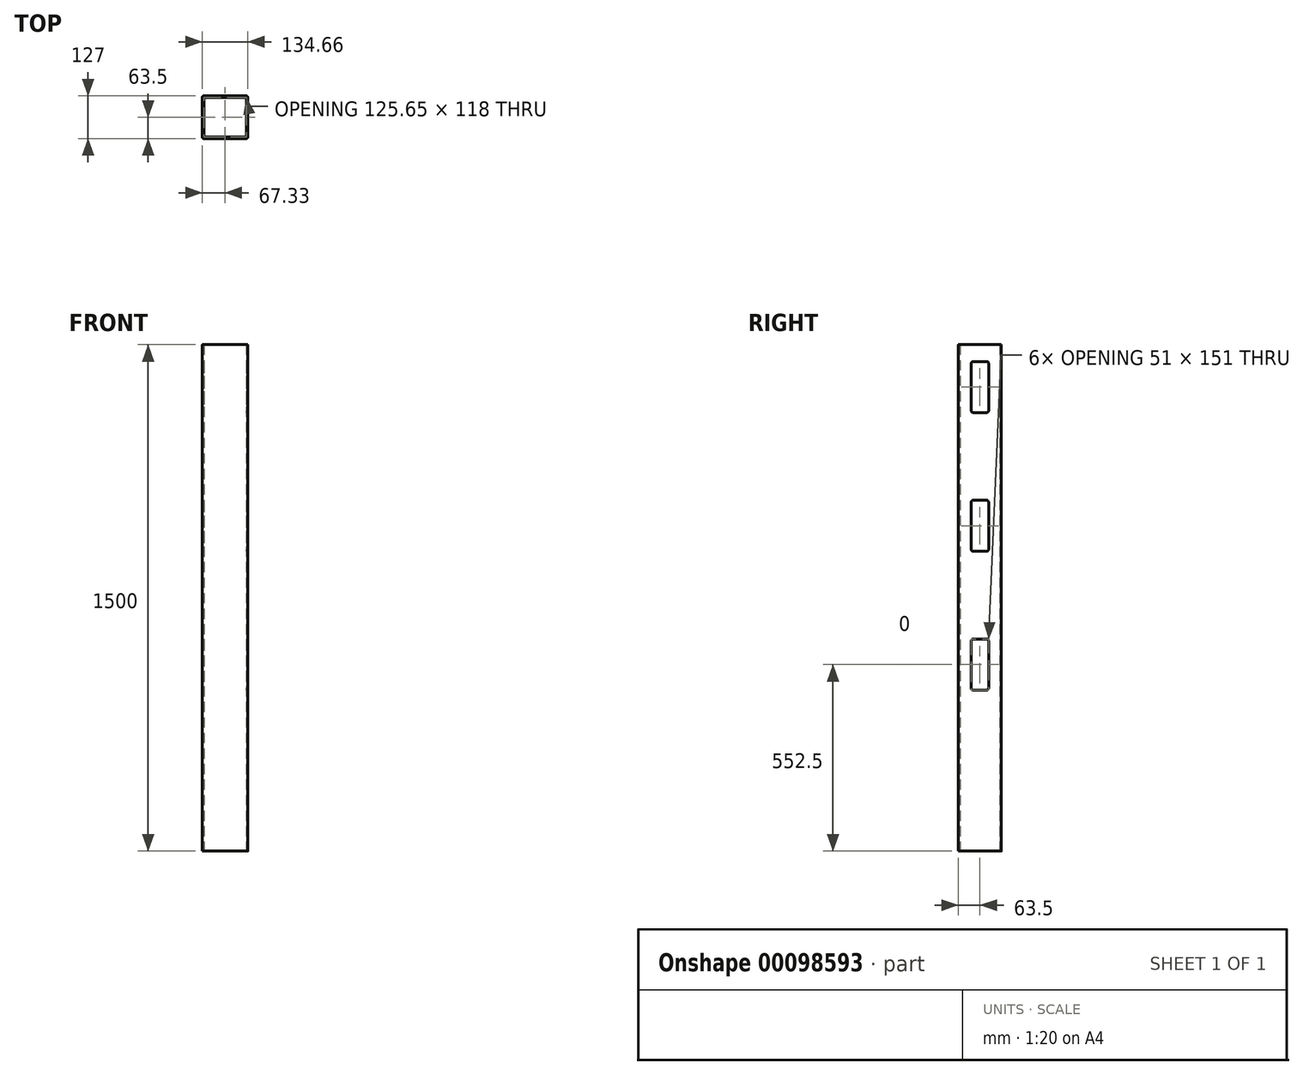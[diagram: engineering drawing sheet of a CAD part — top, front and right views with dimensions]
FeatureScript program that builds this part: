
annotation { "Feature Type Name" : "Feature", "Feature Type Description" : "" }
export const myFeature = defineFeature(function(context is Context, id is Id, definition is map)
    precondition{}
    {
        {
            var Q0;
            Q0=qCreatedBy(makeId("Top.planeOp"),FACE);
            var sketch = newSketch(context, id + "F0", { "sketchPlane" : qUnion([Q0])});
            skLineSegment(sketch, "E0.bottom", {"start": v(62.33, -63.5) * mm, "end": v(-62.33, -63.5) * mm});
            skLineSegment(sketch, "E0.top", {"start": v(62.33, 63.5) * mm, "end": v(-62.33, 63.5) * mm});
            skLineSegment(sketch, "E0.left", {"start": v(67.33, -58.5) * mm, "end": v(67.33, 58.5) * mm});
            skLineSegment(sketch, "E0.right", {"start": v(-67.33, -58.5) * mm, "end": v(-67.33, 58.5) * mm});
            skPoint(sketch, "E0.middle", {"position": v(0, 0) * mm});
            skPoint(sketch, "E1.visualSharp", {"position": v(-67.33, 63.5) * mm});
            skArc(sketch, "E1.filletArc", {"start": v(-62.33, 63.5) * mm, "mid": v(-65.86, 62.04) * mm, "end": v(-67.33, 58.5) * mm});
            skPoint(sketch, "E2.visualSharp", {"position": v(67.33, 63.5) * mm});
            skArc(sketch, "E2.filletArc", {"start": v(67.33, 58.5) * mm, "mid": v(65.86, 62.04) * mm, "end": v(62.33, 63.5) * mm});
            skPoint(sketch, "E3.visualSharp", {"position": v(67.33, -63.5) * mm});
            skArc(sketch, "E3.filletArc", {"start": v(62.33, -63.5) * mm, "mid": v(65.86, -62.04) * mm, "end": v(67.33, -58.5) * mm});
            skPoint(sketch, "E4.visualSharp", {"position": v(-67.33, -63.5) * mm});
            skArc(sketch, "E4.filletArc", {"start": v(-67.33, -58.5) * mm, "mid": v(-65.86, -62.04) * mm, "end": v(-62.33, -63.5) * mm});
            skLineSegment(sketch, "E5.0", {"start": v(57.83, 59) * mm, "end": v(-57.83, 59) * mm});
            skLineSegment(sketch, "E5.1", {"start": v(62.83, -54) * mm, "end": v(62.83, 54) * mm});
            skLineSegment(sketch, "E5.2", {"start": v(57.83, -59) * mm, "end": v(-57.83, -59) * mm});
            skLineSegment(sketch, "E5.3", {"start": v(-62.83, -54) * mm, "end": v(-62.83, 54) * mm});
            skPoint(sketch, "E6.visualSharp", {"position": v(-62.83, 59) * mm});
            skArc(sketch, "E6.filletArc", {"start": v(-57.83, 59) * mm, "mid": v(-61.36, 57.54) * mm, "end": v(-62.83, 54) * mm});
            skPoint(sketch, "E7.visualSharp", {"position": v(62.83, 59) * mm});
            skArc(sketch, "E7.filletArc", {"start": v(62.83, 54) * mm, "mid": v(61.36, 57.54) * mm, "end": v(57.83, 59) * mm});
            skPoint(sketch, "E8.visualSharp", {"position": v(62.83, -59) * mm});
            skArc(sketch, "E8.filletArc", {"start": v(57.83, -59) * mm, "mid": v(61.36, -57.54) * mm, "end": v(62.83, -54) * mm});
            skPoint(sketch, "E9.visualSharp", {"position": v(-62.83, -59) * mm});
            skArc(sketch, "E9.filletArc", {"start": v(-62.83, -54) * mm, "mid": v(-61.36, -57.54) * mm, "end": v(-57.83, -59) * mm});
            skSolve(sketch);
        }
        {
            var Q0;
            Q0=makeQuery(id+"F0.imprint","IMPRINT",FACE,{"disambiguationData":[TD([[makeQuery(id+"F0.imprint","IMPRINT",EDGE,{"derivedFrom":sQuery(id+"F0.wireOp",EDGE,"E0.bottom")}),-1.0]])]});
            extrude(context, id + "F1", {"entities" : qUnion([Q0]), "depth" : 1500 * mm});
        }
        {
            var Q0;
            Q0=makeQuery(id+"F1.opExtrude","SWEPT_FACE",FACE,{"disambiguationData":[OSD([sQuery(id+"F0.wireOp",EDGE,"E0.left")])]});
            var sketch = newSketch(context, id + "F2", { "sketchPlane" : qUnion([Q0])});
            skLineSegment(sketch, "E10.bottom", {"start": v(-20.5, 1299) * mm, "end": v(20.5, 1299) * mm});
            skLineSegment(sketch, "E10.top", {"start": v(-20.5, 1450) * mm, "end": v(20.5, 1450) * mm});
            skLineSegment(sketch, "E10.left", {"start": v(-25.5, 1304) * mm, "end": v(-25.5, 1445) * mm});
            skLineSegment(sketch, "E10.right", {"start": v(25.5, 1304) * mm, "end": v(25.5, 1445) * mm});
            skPoint(sketch, "E10.middle", {"position": v(0, 1374.5) * mm});
            skPoint(sketch, "E10.middle.positionSnap0", {"position": v(0, 1500) * mm});
            skPoint(sketch, "E10.centerSnap0", {"position": v(0, 1500) * mm});
            skPoint(sketch, "E11.visualSharp", {"position": v(25.5, 1450) * mm});
            skArc(sketch, "E11.filletArc", {"start": v(25.5, 1445) * mm, "mid": v(24.04, 1448.54) * mm, "end": v(20.5, 1450) * mm});
            skPoint(sketch, "E12.visualSharp", {"position": v(-25.5, 1450) * mm});
            skArc(sketch, "E12.filletArc", {"start": v(-20.5, 1450) * mm, "mid": v(-24.04, 1448.54) * mm, "end": v(-25.5, 1445) * mm});
            skPoint(sketch, "E13.visualSharp", {"position": v(-25.5, 1299) * mm});
            skArc(sketch, "E13.filletArc", {"start": v(-25.5, 1304) * mm, "mid": v(-24.04, 1300.46) * mm, "end": v(-20.5, 1299) * mm});
            skPoint(sketch, "E14.visualSharp", {"position": v(25.5, 1299) * mm});
            skArc(sketch, "E14.filletArc", {"start": v(20.5, 1299) * mm, "mid": v(24.04, 1300.46) * mm, "end": v(25.5, 1304) * mm});
            skLineSegment(sketch, "E15.bottom", {"start": v(-20.5, 888) * mm, "end": v(20.5, 888) * mm});
            skLineSegment(sketch, "E15.top", {"start": v(-20.5, 1039) * mm, "end": v(20.5, 1039) * mm});
            skLineSegment(sketch, "E15.left", {"start": v(-25.5, 893) * mm, "end": v(-25.5, 1034) * mm});
            skLineSegment(sketch, "E15.right", {"start": v(25.5, 893) * mm, "end": v(25.5, 1034) * mm});
            skArc(sketch, "E16.filletArc", {"start": v(25.5, 1034) * mm, "mid": v(24.04, 1037.54) * mm, "end": v(20.5, 1039) * mm});
            skArc(sketch, "E17.filletArc", {"start": v(-20.5, 1039) * mm, "mid": v(-24.04, 1037.54) * mm, "end": v(-25.5, 1034) * mm});
            skArc(sketch, "E18.filletArc", {"start": v(-25.5, 893) * mm, "mid": v(-24.04, 889.46) * mm, "end": v(-20.5, 888) * mm});
            skArc(sketch, "E19.filletArc", {"start": v(20.5, 888) * mm, "mid": v(24.04, 889.46) * mm, "end": v(25.5, 893) * mm});
            skLineSegment(sketch, "E20.bottom", {"start": v(-20.5, 477) * mm, "end": v(20.5, 477) * mm});
            skLineSegment(sketch, "E20.top", {"start": v(-20.5, 628) * mm, "end": v(20.5, 628) * mm});
            skLineSegment(sketch, "E20.left", {"start": v(-25.5, 482) * mm, "end": v(-25.5, 623) * mm});
            skLineSegment(sketch, "E20.right", {"start": v(25.5, 482) * mm, "end": v(25.5, 623) * mm});
            skArc(sketch, "E21.filletArc", {"start": v(25.5, 623) * mm, "mid": v(24.04, 626.54) * mm, "end": v(20.5, 628) * mm});
            skArc(sketch, "E22.filletArc", {"start": v(-20.5, 628) * mm, "mid": v(-24.04, 626.54) * mm, "end": v(-25.5, 623) * mm});
            skArc(sketch, "E23.filletArc", {"start": v(-25.5, 482) * mm, "mid": v(-24.04, 478.46) * mm, "end": v(-20.5, 477) * mm});
            skArc(sketch, "E24.filletArc", {"start": v(20.5, 477) * mm, "mid": v(24.04, 478.46) * mm, "end": v(25.5, 482) * mm});
            skSolve(sketch);
        }
        {
            var Q0;
            Q0=makeQuery(id+"F2.imprint","IMPRINT",FACE,{"disambiguationData":[TD([[makeQuery(id+"F2.imprint","IMPRINT",EDGE,{"derivedFrom":sQuery(id+"F2.wireOp",EDGE,"E10.bottom")}),-1.0]])]});
            var sketch = newSketch(context, id + "F3", { "sketchPlane" : qUnion([Q0])});
            skSolve(sketch);
        }
        {
            var Q0;
            Q0=makeQuery(id+"F2.imprint","IMPRINT",FACE,{"disambiguationData":[TD([[makeQuery(id+"F2.imprint","IMPRINT",EDGE,{"derivedFrom":sQuery(id+"F2.wireOp",EDGE,"E10.bottom")}),1.0]])]});
            var Q1;
            Q1=makeQuery(id+"F2.imprint","IMPRINT",FACE,{"disambiguationData":[TD([[makeQuery(id+"F2.imprint","IMPRINT",EDGE,{"derivedFrom":sQuery(id+"F2.wireOp",EDGE,"E10.bottom")}),1.0]])]});
            var Q2;
            Q2=makeQuery(id+"F2.imprint","IMPRINT",FACE,{"disambiguationData":[TD([[makeQuery(id+"F2.imprint","IMPRINT",EDGE,{"derivedFrom":sQuery(id+"F2.wireOp",EDGE,"E15.bottom")}),1.0]])]});
            var Q3;
            Q3=makeQuery(id+"F2.imprint","IMPRINT",FACE,{"disambiguationData":[TD([[makeQuery(id+"F2.imprint","IMPRINT",EDGE,{"derivedFrom":sQuery(id+"F2.wireOp",EDGE,"E20.bottom")}),1.0]])]});
            extrude(context, id + "F4", {"entities" : qUnion([Q0, Q1, Q2, Q3]), "operationType" : NewBodyOperationType.REMOVE, "oppositeDirection" : true, "depth" : 150 * mm});
        }
        {
            var Q0;
            Q0=makeQuery(id+"F3.imprint","IMPRINT",FACE,{"disambiguationData":[TD([[makeQuery(id+"F3.imprint","IMPRINT",EDGE,{"derivedFrom":makeQuery(id+"F2.imprint","IMPRINT",EDGE,{"derivedFrom":sQuery(id+"F2.wireOp",EDGE,"E10.bottom")})}),-1.0]])]});
            var sketch = newSketch(context, id + "F5", { "sketchPlane" : qUnion([Q0])});
            skLineSegment(sketch, "E25.bottom", {"start": v(-337.6, 779.85) * mm, "end": v(-377.6, 779.85) * mm});
            skLineSegment(sketch, "E25.top", {"start": v(-337.6, 929.85) * mm, "end": v(-377.6, 929.85) * mm});
            skLineSegment(sketch, "E25.left", {"start": v(-332.6, 784.85) * mm, "end": v(-332.6, 924.85) * mm});
            skLineSegment(sketch, "E25.right", {"start": v(-382.6, 784.85) * mm, "end": v(-382.6, 924.85) * mm});
            skPoint(sketch, "E25.middle", {"position": v(-357.6, 854.85) * mm});
            skPoint(sketch, "E26.visualSharp", {"position": v(-382.6, 929.85) * mm});
            skArc(sketch, "E26.filletArc", {"start": v(-377.6, 929.85) * mm, "mid": v(-381.13, 928.4) * mm, "end": v(-382.6, 924.85) * mm});
            skPoint(sketch, "E27.visualSharp", {"position": v(-332.6, 929.85) * mm});
            skArc(sketch, "E27.filletArc", {"start": v(-332.6, 924.85) * mm, "mid": v(-334.06, 928.4) * mm, "end": v(-337.6, 929.85) * mm});
            skPoint(sketch, "E28.visualSharp", {"position": v(-332.6, 779.85) * mm});
            skArc(sketch, "E28.filletArc", {"start": v(-337.6, 779.85) * mm, "mid": v(-334.06, 781.32) * mm, "end": v(-332.6, 784.85) * mm});
            skPoint(sketch, "E29.visualSharp", {"position": v(-382.6, 779.85) * mm});
            skArc(sketch, "E29.filletArc", {"start": v(-382.6, 784.85) * mm, "mid": v(-381.13, 781.32) * mm, "end": v(-377.6, 779.85) * mm});
            skSolve(sketch);
        }
        {
            var Q0;
            Q0=makeQuery(id+"F5.imprint","IMPRINT",FACE,{"disambiguationData":[TD([[makeQuery(id+"F5.imprint","IMPRINT",EDGE,{"derivedFrom":sQuery(id+"F5.wireOp",EDGE,"E25.bottom")}),-1.0]])]});
            var sketch = newSketch(context, id + "F6", { "sketchPlane" : qUnion([Q0])});
            skArc(sketch, "E30.0", {"start": v(-335.1, 924.85) * mm, "mid": v(-335.82, 926.62) * mm, "end": v(-337.6, 927.35) * mm});
            skLineSegment(sketch, "E30.1", {"start": v(-335.1, 784.85) * mm, "end": v(-335.1, 829.35) * mm});
            skLineSegment(sketch, "E30.2", {"start": v(-337.6, 927.35) * mm, "end": v(-377.6, 927.35) * mm});
            skArc(sketch, "E30.3", {"start": v(-337.6, 782.35) * mm, "mid": v(-335.82, 783.09) * mm, "end": v(-335.1, 784.85) * mm});
            skArc(sketch, "E30.4", {"start": v(-377.6, 927.35) * mm, "mid": v(-379.36, 926.62) * mm, "end": v(-380.1, 924.85) * mm});
            skLineSegment(sketch, "E30.5", {"start": v(-380.1, 784.85) * mm, "end": v(-380.1, 829.35) * mm});
            skArc(sketch, "E30.6", {"start": v(-380.1, 784.85) * mm, "mid": v(-379.36, 783.09) * mm, "end": v(-377.6, 782.35) * mm});
            skLineSegment(sketch, "E30.7", {"start": v(-337.6, 782.35) * mm, "end": v(-377.6, 782.35) * mm});
            skLineSegment(sketch, "E31", {"start": v(-380.1, 880.35) * mm, "end": v(-335.1, 880.35) * mm});
            skLineSegment(sketch, "E32", {"start": v(-380.1, 829.35) * mm, "end": v(-335.1, 829.35) * mm});
            skLineSegment(sketch, "E33.0", {"start": v(-380.1, 878.35) * mm, "end": v(-335.1, 878.35) * mm});
            skLineSegment(sketch, "E34.0", {"start": v(-380.1, 831.35) * mm, "end": v(-335.1, 831.35) * mm});
            skLineSegment(sketch, "E35.trimOffspring", {"start": v(-335.1, 880.35) * mm, "end": v(-335.1, 924.85) * mm});
            skLineSegment(sketch, "E36.trimOffspring", {"start": v(-380.1, 880.35) * mm, "end": v(-380.1, 924.85) * mm});
            skLineSegment(sketch, "E37.trimOffspring", {"start": v(-335.1, 831.35) * mm, "end": v(-335.1, 878.35) * mm});
            skLineSegment(sketch, "E38.trimOffspring", {"start": v(-380.1, 831.35) * mm, "end": v(-380.1, 878.35) * mm});
            skSolve(sketch);
        }
        {
            var Q0;
            Q0 = qSketchRegion(id + "F6", true);
            var Q1;
            Q1=sQuery(id+"F5.wireOp",EDGE,"E25.left");
            var Q2;
            Q2=sQuery(id+"F6.wireOp",EDGE,"E35.trimOffspring");
            var Q3;
            Q3=sQuery(id+"F5.wireOp",EDGE,"E25.right");
            var Q4;
            Q4=sQuery(id+"F6.wireOp",EDGE,"E38.trimOffspring");
            var Q5;
            Q5=sQuery(id+"F6.wireOp",EDGE,"E30.4");
            var Q6;
            Q6=sQuery(id+"F6.wireOp",EDGE,"E30.2");
            var Q7;
            Q7=sQuery(id+"F5.wireOp",EDGE,"E25.top");
            var Q8;
            Q8=sQuery(id+"F5.wireOp",EDGE,"E26.filletArc");
            var Q9;
            Q9=sQuery(id+"F6.wireOp",EDGE,"E36.trimOffspring");
            var Q10;
            Q10=sQuery(id+"F6.wireOp",EDGE,"E33.0");
            var Q11;
            Q11=sQuery(id+"F6.wireOp",EDGE,"E31");
            var Q12;
            Q12=sQuery(id+"F5.wireOp",EDGE,"E27.filletArc");
            var Q13;
            Q13=sQuery(id+"F6.wireOp",EDGE,"E30.0");
            var Q14;
            Q14=sQuery(id+"F6.wireOp",EDGE,"E37.trimOffspring");
            var Q15;
            Q15=sQuery(id+"F6.wireOp",EDGE,"E34.0");
            var Q16;
            Q16=sQuery(id+"F6.wireOp",EDGE,"E32");
            var Q17;
            Q17=sQuery(id+"F6.wireOp",EDGE,"E30.1");
            var Q18;
            Q18=sQuery(id+"F6.wireOp",EDGE,"E30.3");
            var Q19;
            Q19=sQuery(id+"F5.wireOp",EDGE,"E28.filletArc");
            var Q20;
            Q20=sQuery(id+"F5.wireOp",EDGE,"E25.bottom");
            var Q21;
            Q21=sQuery(id+"F6.wireOp",EDGE,"E30.7");
            var Q22;
            Q22=sQuery(id+"F6.wireOp",EDGE,"E30.6");
            var Q23;
            Q23=sQuery(id+"F5.wireOp",EDGE,"E29.filletArc");
            var Q24;
            Q24=sQuery(id+"F6.wireOp",EDGE,"E30.5");
            extrude(context, id + "F7", {"entities" : qUnion([Q0]), "bodyType" : ToolBodyType.SURFACE, "operationType" : NewBodyOperationType.ADD, "surfaceEntities" : qUnion([Q1, Q2, Q3, Q4, Q5, Q6, Q7, Q8, Q9, Q10, Q11, Q12, Q13, Q14, Q15, Q16, Q17, Q18, Q19, Q20, Q21, Q22, Q23, Q24]), "depth" : 1200 * mm, "hasSecondDirection" : true, "secondDirectionOppositeDirection" : true, "secondDirectionDepth" : 1200 * mm});
        }
    });
